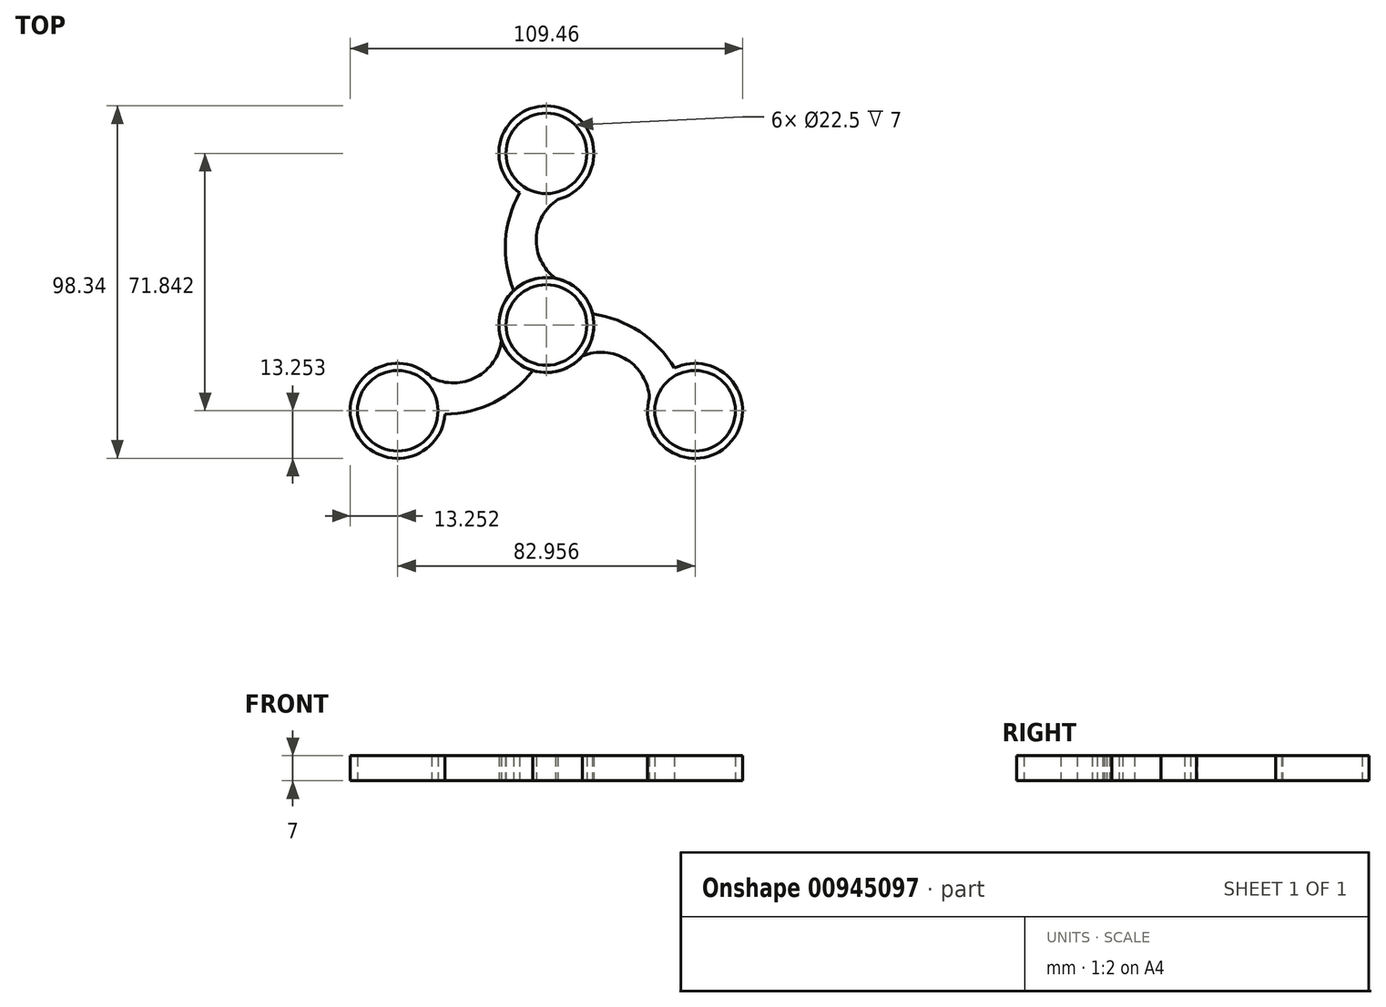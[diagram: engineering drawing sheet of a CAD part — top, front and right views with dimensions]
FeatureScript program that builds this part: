
annotation { "Feature Type Name" : "Feature", "Feature Type Description" : "" }
export const myFeature = defineFeature(function(context is Context, id is Id, definition is map)
    precondition{}
    {
        {
            var Q0;
            Q0=qCreatedBy(makeId("Top.planeOp"),FACE);
            var sketch = newSketch(context, id + "F0", { "sketchPlane" : qUnion([Q0])});
            skCircle(sketch, "E0", {"center": v(0, 0) * mm, "radius": 11.25 * mm});
            skCircle(sketch, "E1.0", {"center": v(0, 0) * mm, "radius": 13.25 * mm});
            skCircle(sketch, "E2", {"center": v(0, 47.9) * mm, "radius": 11.25 * mm});
            skCircle(sketch, "E3.0", {"center": v(0, 47.9) * mm, "radius": 13.25 * mm});
            skArc(sketch, "E4", {"start": v(-7.44, 36.93) * mm, "mid": v(-11.4, 23.46) * mm, "end": v(-9.12, 9.61) * mm});
            skArc(sketch, "E5", {"start": v(7.32, 36.85) * mm, "mid": v(-2.57, 26.44) * mm, "end": v(2.5, 13.01) * mm});
            skSolve(sketch);
        }
        {
            var Q0;
            Q0 = qSketchRegion(id + "F0", true);
            extrude(context, id + "F1", {"entities" : qUnion([Q0]), "depth" : 7 * mm, "offsetDistance" : 25 * mm});
        }
        {
            var Q0;
            Q0=makeQuery(id+"F1.opExtrude","SWEPT_BODY",BODY,{"disambiguationData":[OSD([sQuery(id+"F0.wireOp",EDGE,"E0"),sQuery(id+"F0.wireOp",EDGE,"E1.0"),sQuery(id+"F0.wireOp",EDGE,"E2"),sQuery(id+"F0.wireOp",EDGE,"E3.0"),sQuery(id+"F0.wireOp",EDGE,"E4"),sQuery(id+"F0.wireOp",EDGE,"E5")])]});
            var Q1;
            Q1=makeQuery(id+"F1.opExtrude","CAP_EDGE",EDGE,{"disambiguationData":[OSD([sQuery(id+"F0.wireOp",EDGE,"E0")])],"isStart":false});
            circularPattern(context, id + "F2", {"entities" : qUnion([Q0]), "axis" : qUnion([Q1]), "angle" : 360 * degree, "instanceCount" : 3, "equalSpace" : true});
        }
    });
